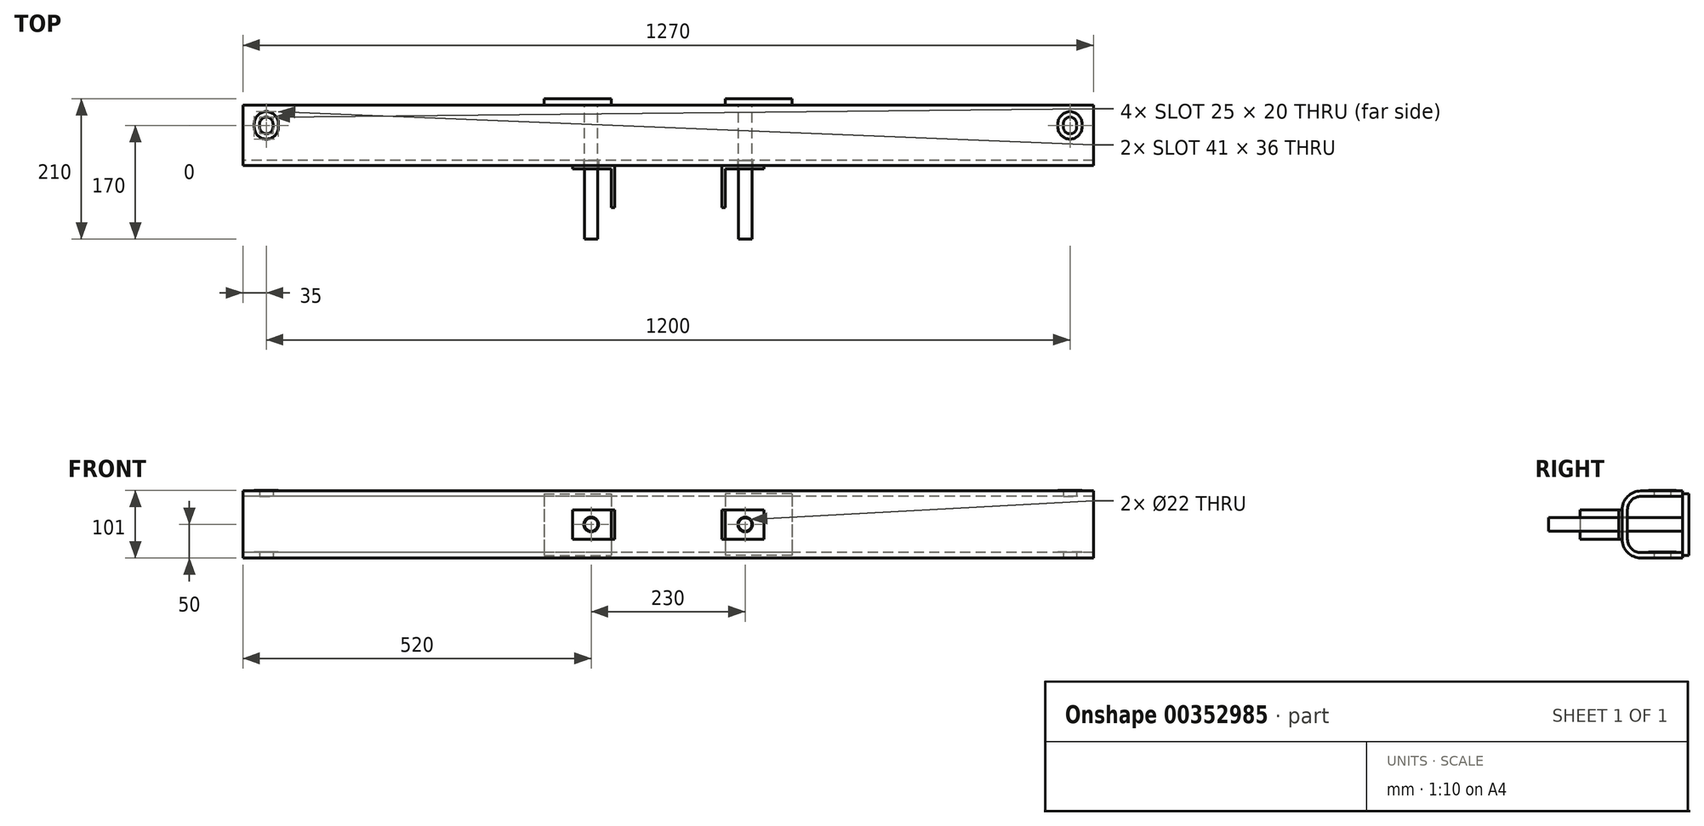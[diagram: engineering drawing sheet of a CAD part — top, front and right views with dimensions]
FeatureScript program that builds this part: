
annotation { "Feature Type Name" : "Feature", "Feature Type Description" : "" }
export const myFeature = defineFeature(function(context is Context, id is Id, definition is map)
    precondition{}
    {
        {
            var Q0;
            Q0=qCreatedBy(makeId("Right.planeOp"),FACE);
            var sketch = newSketch(context, id + "F0", { "sketchPlane" : qUnion([Q0])});
            skLineSegment(sketch, "E0", {"start": v(90, 50) * mm, "end": v(28, 50) * mm});
            skLineSegment(sketch, "E1", {"start": v(0, 22) * mm, "end": v(0, -22) * mm});
            skLineSegment(sketch, "E2", {"start": v(28, -50) * mm, "end": v(90, -50) * mm});
            skLineSegment(sketch, "E3", {"start": v(90, -50) * mm, "end": v(90, -42) * mm});
            skLineSegment(sketch, "E4", {"start": v(90, -42) * mm, "end": v(28, -42) * mm});
            skLineSegment(sketch, "E5", {"start": v(8, -22) * mm, "end": v(8, 22) * mm});
            skLineSegment(sketch, "E6", {"start": v(28, 42) * mm, "end": v(90, 42) * mm});
            skLineSegment(sketch, "E7", {"start": v(90, 42) * mm, "end": v(90, 50) * mm});
            skPoint(sketch, "E8.visualSharp", {"position": v(8, 42) * mm});
            skArc(sketch, "E8.filletArc", {"start": v(28, 42) * mm, "mid": v(13.86, 36.14) * mm, "end": v(8, 22) * mm});
            skPoint(sketch, "E9.visualSharp", {"position": v(8, -42) * mm});
            skArc(sketch, "E9.filletArc", {"start": v(8, -22) * mm, "mid": v(13.86, -36.14) * mm, "end": v(28, -42) * mm});
            skPoint(sketch, "E10.visualSharp", {"position": v(0, 50) * mm});
            skArc(sketch, "E10.filletArc", {"start": v(28, 50) * mm, "mid": v(8.2, 41.8) * mm, "end": v(0, 22) * mm});
            skPoint(sketch, "E11.visualSharp", {"position": v(0, -50) * mm});
            skArc(sketch, "E11.filletArc", {"start": v(0, -22) * mm, "mid": v(8.2, -41.8) * mm, "end": v(28, -50) * mm});
            skSolve(sketch);
        }
        {
            var Q0;
            Q0=qSketchRegion(id+"F0",true);
            extrude(context, id + "F1", {"entities" : qUnion([Q0]), "endBound" : BoundingType.SYMMETRIC, "depth" : 1270 * mm});
        }
        {
            var Q0;
            Q0=qCreatedBy(makeId("Top.planeOp"),FACE);
            var sketch = newSketch(context, id + "F2", { "sketchPlane" : qUnion([Q0])});
            skLineSegment(sketch, "E12", {"start": v(-143, 0) * mm, "end": v(-80, 0) * mm});
            skLineSegment(sketch, "E13", {"start": v(-80, 0) * mm, "end": v(-80, -63) * mm});
            skLineSegment(sketch, "E14.0", {"start": v(-85, -5) * mm, "end": v(-85, -63) * mm});
            skLineSegment(sketch, "E14.1", {"start": v(-143, -5) * mm, "end": v(-85, -5) * mm});
            skLineSegment(sketch, "E15", {"start": v(-143, -5) * mm, "end": v(-143, 0) * mm});
            skLineSegment(sketch, "E16", {"start": v(-85, -63) * mm, "end": v(-80, -63) * mm});
            skLineSegment(sketch, "E17.MirrorCS", {"start": v(85, -63) * mm, "end": v(80, -63) * mm});
            skLineSegment(sketch, "E18.MirrorCS", {"start": v(143, -5) * mm, "end": v(143, 0) * mm});
            skLineSegment(sketch, "E19.MirrorCS", {"start": v(143, 0) * mm, "end": v(80, 0) * mm});
            skLineSegment(sketch, "E20.MirrorCS", {"start": v(80, 0) * mm, "end": v(80, -63) * mm});
            skLineSegment(sketch, "E21.MirrorCS", {"start": v(143, -5) * mm, "end": v(85, -5) * mm});
            skLineSegment(sketch, "E22.MirrorCS", {"start": v(85, -5) * mm, "end": v(85, -63) * mm});
            skSolve(sketch);
        }
        {
            var Q0;
            Q0=qSketchRegion(id+"F2",true);
            extrude(context, id + "F3", {"entities" : qUnion([Q0]), "operationType" : NewBodyOperationType.ADD, "endBound" : BoundingType.SYMMETRIC, "depth" : 44 * mm});
        }
        {
            var Q0;
            Q0=makeQuery(id+"F1.opExtrude","SWEPT_FACE",FACE,{"disambiguationData":[OSD([sQuery(id+"F0.wireOp",EDGE,"E7")])]});
            var sketch = newSketch(context, id + "F4", { "sketchPlane" : qUnion([Q0])});
            skLineSegment(sketch, "E23.bottom", {"start": v(-185, 46) * mm, "end": v(-85, 46) * mm});
            skLineSegment(sketch, "E23.top", {"start": v(-185, -46) * mm, "end": v(-85, -46) * mm});
            skLineSegment(sketch, "E23.left", {"start": v(-185, 46) * mm, "end": v(-185, -46) * mm});
            skLineSegment(sketch, "E23.right", {"start": v(-85, 46) * mm, "end": v(-85, -46) * mm});
            skLineSegment(sketch, "E24.MirrorCS", {"start": v(85, 46) * mm, "end": v(85, -46) * mm});
            skLineSegment(sketch, "E25.MirrorCS", {"start": v(185, 46) * mm, "end": v(185, -46) * mm});
            skLineSegment(sketch, "E26.MirrorCS", {"start": v(185, 46) * mm, "end": v(85, 46) * mm});
            skLineSegment(sketch, "E27.MirrorCS", {"start": v(185, -46) * mm, "end": v(85, -46) * mm});
            skSolve(sketch);
        }
        {
            var Q0;
            Q0=qSketchRegion(id+"F4",true);
            extrude(context, id + "F5", {"entities" : qUnion([Q0]), "operationType" : NewBodyOperationType.ADD, "depth" : 10 * mm});
        }
        {
            var Q0;
            Q0=qCreatedBy(makeId("Front.planeOp"),FACE);
            var sketch = newSketch(context, id + "F6", { "sketchPlane" : qUnion([Q0])});
            skCircle(sketch, "E28", {"center": v(-115, 0) * mm, "radius": 11 * mm});
            skCircle(sketch, "E29.MirrorC", {"center": v(115, 0) * mm, "radius": 11 * mm});
            skSolve(sketch);
        }
        {
            var Q0;
            Q0=qSketchRegion(id+"F6",true);
            extrude(context, id + "F7", {"entities" : qUnion([Q0]), "operationType" : NewBodyOperationType.REMOVE, "endBound" : BoundingType.UP_TO_NEXT, "oppositeDirection" : true, "depth" : 25 * mm, "hasSecondDirection" : true, "secondDirectionBound" : SecondDirectionBoundingType.THROUGH_ALL, "secondDirectionOppositeDirection" : false, "secondDirectionDepth" : 25 * mm});
        }
        {
            var Q0;
            Q0=qCreatedBy(makeId("Top.planeOp"),FACE);
            var sketch = newSketch(context, id + "F8", { "sketchPlane" : qUnion([Q0])});
            skArc(sketch, "E30", {"start": v(-590, 62.5) * mm, "mid": v(-600, 72.5) * mm, "end": v(-610, 62.5) * mm});
            skLineSegment(sketch, "E31", {"start": v(-610, 62.5) * mm, "end": v(-610, 57.5) * mm});
            skLineSegment(sketch, "E32", {"start": v(-590, 62.5) * mm, "end": v(-590, 57.5) * mm});
            skArc(sketch, "E33", {"start": v(-610, 57.5) * mm, "mid": v(-600, 47.5) * mm, "end": v(-590, 57.5) * mm});
            skLineSegment(sketch, "E34.MirrorCS", {"start": v(590, 62.5) * mm, "end": v(590, 57.5) * mm});
            skLineSegment(sketch, "E35.MirrorCS", {"start": v(610, 62.5) * mm, "end": v(610, 57.5) * mm});
            skArc(sketch, "E36.MirrorCS", {"start": v(610, 57.5) * mm, "mid": v(600, 47.5) * mm, "end": v(590, 57.5) * mm});
            skArc(sketch, "E37.MirrorCS", {"start": v(590, 62.5) * mm, "mid": v(600, 72.5) * mm, "end": v(610, 62.5) * mm});
            skSolve(sketch);
        }
        {
            var Q0;
            Q0=qSketchRegion(id+"F8",true);
            extrude(context, id + "F9", {"entities" : qUnion([Q0]), "operationType" : NewBodyOperationType.REMOVE, "endBound" : BoundingType.THROUGH_ALL, "depth" : 25 * mm, "hasSecondDirection" : true, "secondDirectionBound" : SecondDirectionBoundingType.THROUGH_ALL, "secondDirectionOppositeDirection" : true, "secondDirectionDepth" : 25 * mm});
        }
        {
            var Q0;
            Q0=makeQuery(id+"F1.opExtrude","SWEPT_FACE",FACE,{"disambiguationData":[OSD([sQuery(id+"F0.wireOp",EDGE,"E0")])]});
            var sketch = newSketch(context, id + "F10", { "sketchPlane" : qUnion([Q0])});
            skLineSegment(sketch, "E38", {"start": v(-610, 62.5) * mm, "end": v(-610, 57.5) * mm});
            skLineSegment(sketch, "E39", {"start": v(-590, 57.5) * mm, "end": v(-590, 62.5) * mm});
            skArc(sketch, "E40", {"start": v(-590, 62.5) * mm, "mid": v(-600, 72.5) * mm, "end": v(-610, 62.5) * mm});
            skArc(sketch, "E41", {"start": v(-610, 57.5) * mm, "mid": v(-600, 47.5) * mm, "end": v(-590, 57.5) * mm});
            skArc(sketch, "E42.0", {"start": v(-582, 62.5) * mm, "mid": v(-600, 80.5) * mm, "end": v(-618, 62.5) * mm});
            skLineSegment(sketch, "E42.1", {"start": v(-582, 57.5) * mm, "end": v(-582, 62.5) * mm});
            skArc(sketch, "E42.2", {"start": v(-618, 57.5) * mm, "mid": v(-600, 39.5) * mm, "end": v(-582, 57.5) * mm});
            skLineSegment(sketch, "E42.3", {"start": v(-618, 62.5) * mm, "end": v(-618, 57.5) * mm});
            skLineSegment(sketch, "E43.MirrorCS", {"start": v(590, 57.5) * mm, "end": v(590, 62.5) * mm});
            skLineSegment(sketch, "E44.MirrorCS", {"start": v(610, 62.5) * mm, "end": v(610, 57.5) * mm});
            skLineSegment(sketch, "E45.MirrorCS", {"start": v(618, 62.5) * mm, "end": v(618, 57.5) * mm});
            skLineSegment(sketch, "E46.MirrorCS", {"start": v(582, 57.5) * mm, "end": v(582, 62.5) * mm});
            skArc(sketch, "E47.MirrorCS", {"start": v(590, 62.5) * mm, "mid": v(600, 72.5) * mm, "end": v(610, 62.5) * mm});
            skArc(sketch, "E48.MirrorCS", {"start": v(610, 57.5) * mm, "mid": v(600, 47.5) * mm, "end": v(590, 57.5) * mm});
            skArc(sketch, "E49.MirrorCS", {"start": v(582, 62.5) * mm, "mid": v(600, 80.5) * mm, "end": v(618, 62.5) * mm});
            skArc(sketch, "E50.MirrorCS", {"start": v(618, 57.5) * mm, "mid": v(600, 39.5) * mm, "end": v(582, 57.5) * mm});
            skSolve(sketch);
        }
        {
            var Q0;
            Q0=qSketchRegion(id+"F10",true);
            extrude(context, id + "F11", {"entities" : qUnion([Q0]), "operationType" : NewBodyOperationType.ADD, "depth" : 1 * mm});
        }
        {
            var Q0;
            Q0=makeQuery(id+"F1.opExtrude","SWEPT_FACE",FACE,{"disambiguationData":[OSD([sQuery(id+"F0.wireOp",EDGE,"E4")])]});
            var sketch = newSketch(context, id + "F12", { "sketchPlane" : qUnion([Q0])});
            skLineSegment(sketch, "E51", {"start": v(-610, 62.5) * mm, "end": v(-610, 57.5) * mm});
            skLineSegment(sketch, "E52", {"start": v(-590, 62.5) * mm, "end": v(-590, 57.5) * mm});
            skArc(sketch, "E53", {"start": v(-590, 62.5) * mm, "mid": v(-600, 72.5) * mm, "end": v(-610, 62.5) * mm});
            skArc(sketch, "E54", {"start": v(-610, 57.5) * mm, "mid": v(-600, 47.5) * mm, "end": v(-590, 57.5) * mm});
            skLineSegment(sketch, "E55.0", {"start": v(-618, 62.5) * mm, "end": v(-618, 57.5) * mm});
            skArc(sketch, "E55.1", {"start": v(-582, 62.5) * mm, "mid": v(-600, 80.5) * mm, "end": v(-618, 62.5) * mm});
            skLineSegment(sketch, "E55.2", {"start": v(-582, 62.5) * mm, "end": v(-582, 57.5) * mm});
            skArc(sketch, "E55.3", {"start": v(-618, 57.5) * mm, "mid": v(-600, 39.5) * mm, "end": v(-582, 57.5) * mm});
            skLineSegment(sketch, "E56.MirrorCS", {"start": v(610, 62.5) * mm, "end": v(610, 57.5) * mm});
            skLineSegment(sketch, "E57.MirrorCS", {"start": v(590, 62.5) * mm, "end": v(590, 57.5) * mm});
            skLineSegment(sketch, "E58.MirrorCS", {"start": v(582, 62.5) * mm, "end": v(582, 57.5) * mm});
            skLineSegment(sketch, "E59.MirrorCS", {"start": v(618, 62.5) * mm, "end": v(618, 57.5) * mm});
            skArc(sketch, "E60.MirrorCS", {"start": v(590, 62.5) * mm, "mid": v(600, 72.5) * mm, "end": v(610, 62.5) * mm});
            skArc(sketch, "E61.MirrorCS", {"start": v(610, 57.5) * mm, "mid": v(600, 47.5) * mm, "end": v(590, 57.5) * mm});
            skArc(sketch, "E62.MirrorCS", {"start": v(582, 62.5) * mm, "mid": v(600, 80.5) * mm, "end": v(618, 62.5) * mm});
            skArc(sketch, "E63.MirrorCS", {"start": v(618, 57.5) * mm, "mid": v(600, 39.5) * mm, "end": v(582, 57.5) * mm});
            skSolve(sketch);
        }
        {
            var Q0;
            Q0=qSketchRegion(id+"F12",true);
            extrude(context, id + "F13", {"entities" : qUnion([Q0]), "operationType" : NewBodyOperationType.ADD, "depth" : 1 * mm});
        }
        {
            var Q0;
            Q0=makeQuery(id+"F5.opExtrude","CAP_FACE",FACE,{"disambiguationData":[OSD([sQuery(id+"F4.wireOp",EDGE,"E24.MirrorCS"),sQuery(id+"F4.wireOp",EDGE,"E25.MirrorCS"),sQuery(id+"F4.wireOp",EDGE,"E26.MirrorCS"),sQuery(id+"F4.wireOp",EDGE,"E27.MirrorCS")])],"isStart":true});
            var sketch = newSketch(context, id + "F14", { "sketchPlane" : qUnion([Q0])});
            skCircle(sketch, "E64", {"center": v(-115, 0) * mm, "radius": 10 * mm});
            skCircle(sketch, "E65.MirrorC", {"center": v(115, 0) * mm, "radius": 10 * mm});
            skSolve(sketch);
        }
        {
            var Q0;
            Q0 = qSketchRegion(id + "F14", true);
            extrude(context, id + "F15", {"entities" : qUnion([Q0]), "operationType" : NewBodyOperationType.ADD, "depth" : 200 * mm});
        }
    });
